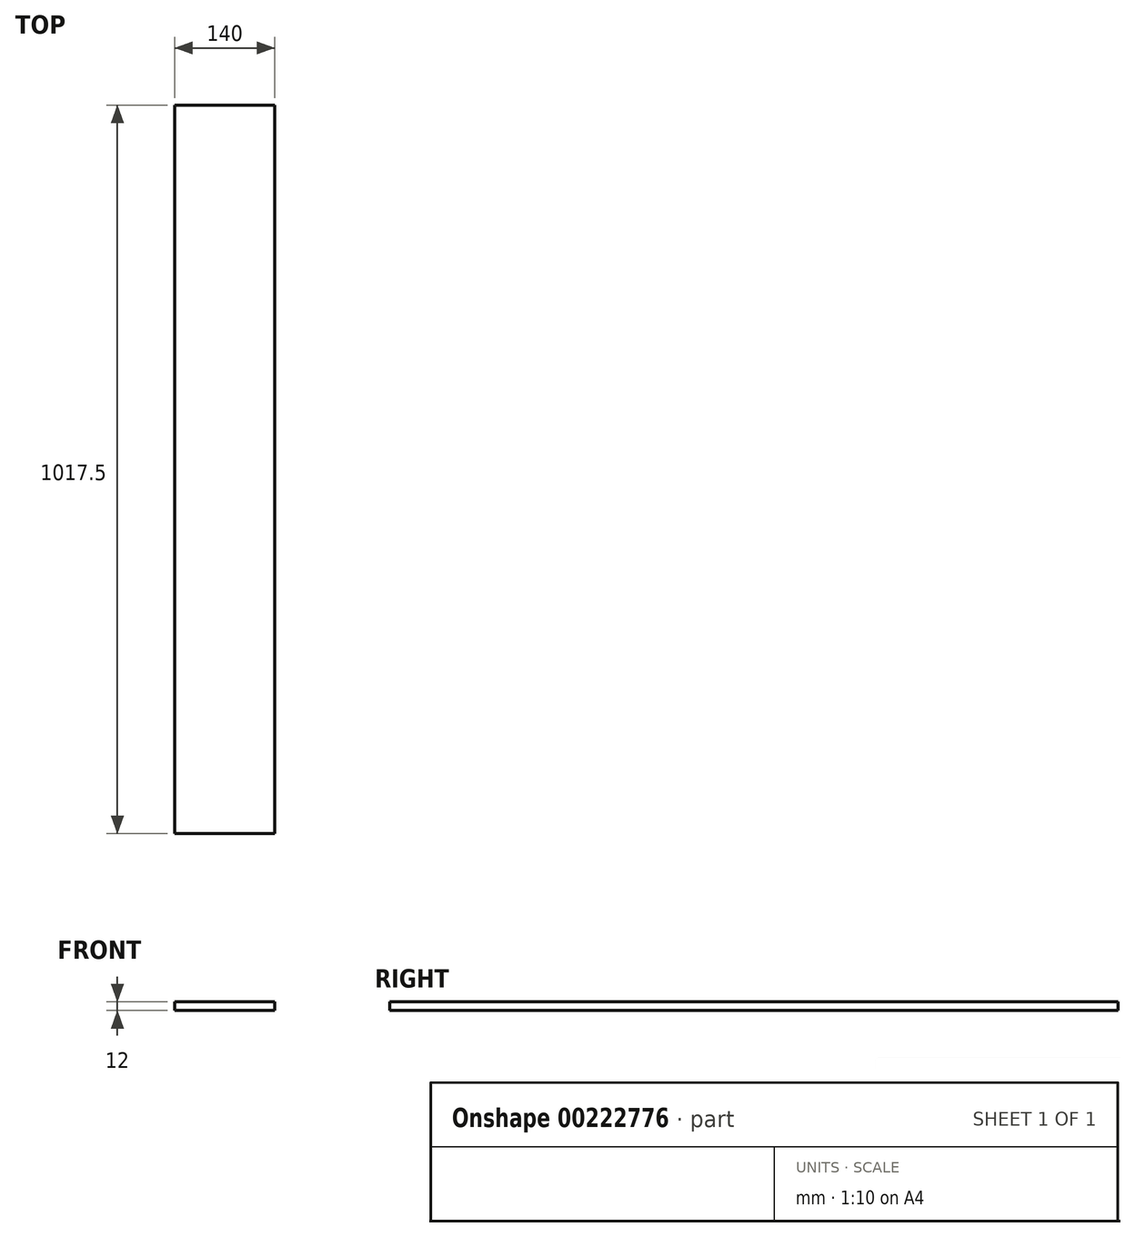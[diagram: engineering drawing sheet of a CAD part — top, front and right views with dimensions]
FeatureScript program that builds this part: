
annotation { "Feature Type Name" : "Feature", "Feature Type Description" : "" }
export const myFeature = defineFeature(function(context is Context, id is Id, definition is map)
    precondition{}
    {
        {
            var Q0;
            Q0=qCreatedBy(makeId("Top.planeOp"),FACE);
            var sketch = newSketch(context, id + "F0", { "sketchPlane" : qUnion([Q0])});
            skLineSegment(sketch, "E0.bottom", {"start": v(0, 0) * mm, "end": v(140, 0) * mm});
            skLineSegment(sketch, "E0.top", {"start": v(0, 1017.5) * mm, "end": v(140, 1017.5) * mm});
            skLineSegment(sketch, "E0.left", {"start": v(0, 0) * mm, "end": v(0, 1017.5) * mm});
            skLineSegment(sketch, "E0.right", {"start": v(140, 0) * mm, "end": v(140, 1017.5) * mm});
            skSolve(sketch);
        }
        {
            var Q0;
            Q0=qSketchRegion(id+"F0",true);
            extrude(context, id + "F1", {"entities" : qUnion([Q0]), "depth" : 12 * mm});
        }
    });
